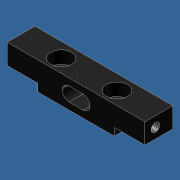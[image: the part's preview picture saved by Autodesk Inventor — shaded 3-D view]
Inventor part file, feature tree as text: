
AUTODESK INVENTOR PART (.ipt)
format: ipt  version: unknown  size: 244,736 bytes
history: native  units: in
note: dims shown in document units (in); Inventor stores cm internally (conversion verified against a paired STEP export)
features: sketch x7, hole x4, extrude x3, fillet x1
ambient origin geometry x8: Origin, YZ Plane, XZ Plane, XY Plane, X Axis, Y Axis, Z Axis, Center Point
bodies: Solid1 (feature_tree)
feature tree (15):
  extrude  "Extrusion1"  Depth=0.5in
  hole  "Hole1"  [1 undecoded]
  extrude  "Extrusion2"  Depth=0.1375in
  hole  "Hole2"  [1 undecoded]
  hole  "Hole3"  [1 undecoded]
  extrude  "Extrusion3"  Depth=0.1812in
  fillet  "Fillet1"  Radius=0.5in
  hole  "Hole5"  [1 undecoded]
  sketch  "Sketch1"  dims[d0=2.475in d1=0.5in]
  sketch  "Sketch2"  dims[d2=0.5in d3=0.0in d6=0.5in]
  sketch  "Sketch3"  dims[d7=0.5in]
  sketch  "Sketch4"  dims[d8=0.196in d9=0.75in d10=0.375in d11=0.25in d12=0.5635in d13=1.0in d14=0.8108in d15=0.1375in]
  sketch  "Sketch5"  dims[d16=0.55in d17=0.1375in]
  sketch  "Sketch6"  dims[d18=0.55in d19=1.0in d20=0.0in]
  sketch  "Sketch8"  dims[d21=0.1812in d23=0.156in d24=0.375in d25=0.375in d26=0.25in d27=0.5635in d28=0.5in d29=0.8108in d31=0.1812in d32=0.156in d33=0.375in d34=0.375in d35=0.25in d36=0.5635in d37=0.5in d38=0.8108in d39=0.5in d40=0.25in d41=0.4375in d42=0.125in d43=1.0in d44=0.0in d45=0.125in d55=0.188in d56=0.234in d57=0.234in d58=0.201in d59=0.75in d60=0.375in d61=0.225in d62=0.5635in d63=1.0in d64=0.8108in d65=0.4375in d66=0.188in]
note: 4 required parameter values undecoded (feature->parameter linkage not recoverable at this tier; creation-order binding heuristic only, values carry confidence <= 0.55)
